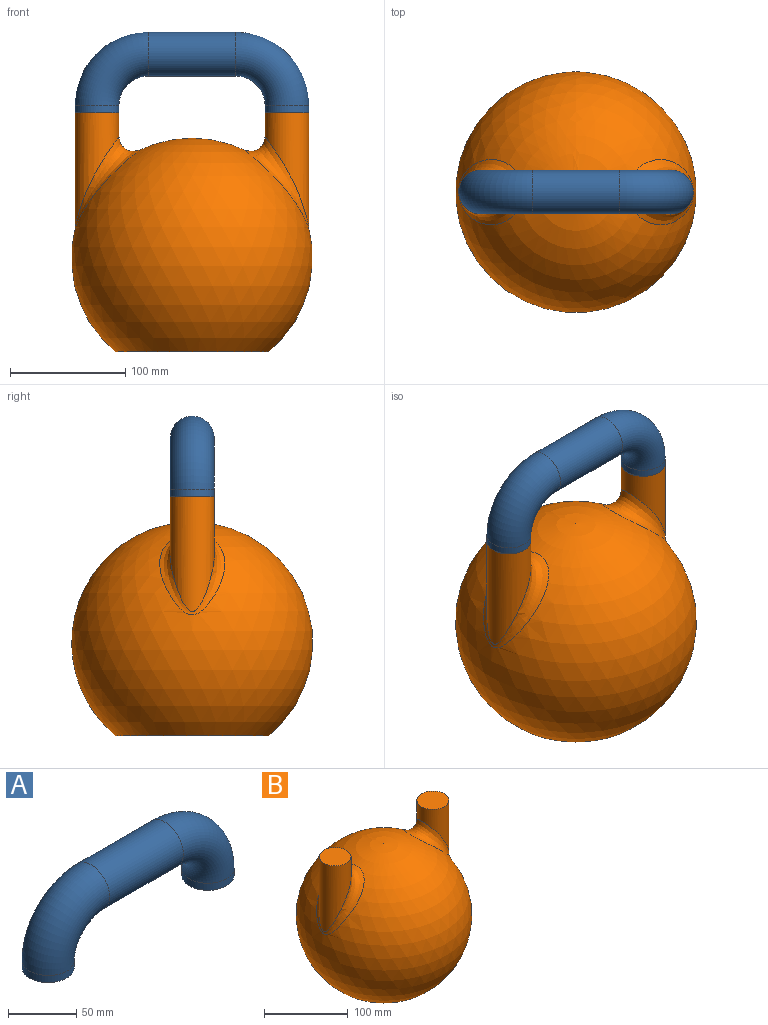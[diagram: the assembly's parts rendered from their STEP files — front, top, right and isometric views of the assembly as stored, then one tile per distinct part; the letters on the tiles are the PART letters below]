
ASSEMBLY  parts=2 mates=1
PART A: 7 faces, bbox 213.7x38.1x75.1 mm
  f0: plane 38.1x38.1mm, normal (0,0,-1), area 1140.1mm2, adj f2
  f1: plane 38.1x38.1mm, normal (0,0,-1), area 1140.1mm2, adj f6
  f2: cylinder r=19.05mm len=38.1mm, axis (0,0,1), area 760.1mm2, adj f0,f3
  f3: torus R=44.45mm, axis (0,1,0), area 8357.3mm2, adj f2,f4
  f4: cylinder r=19.05mm len=76.2mm, axis (1,0,0), area 9120.7mm2, adj f3,f5
  f5: torus R=44.45mm, axis (0,1,0), area 8357.3mm2, adj f4,f6
  f6: cylinder r=19.05mm len=38.1mm, axis (0,0,-1), area 760.1mm2, adj f1,f5
PART B: 8 faces, bbox 209.6x209.6x207.8 mm
  f0: sphere r=104.77mm, area 114109.8mm2, adj f1,f4,f7
  f1: plane 133.35x133.35mm, normal (0,0,-1), area 13966.1mm2, adj f0
  f2: cylinder r=19.05mm len=99.88mm, axis (0,0,-1), area 6523.3mm2, adj f3,f4
  f3: plane 38.1x38.1mm, normal (0,0,1), area 1140.1mm2, adj f2
  f4: bspline ~81.75x56.69mm, area 2989.2mm2, adj f0,f2
  f5: cylinder r=19.05mm len=99.88mm, axis (0,0,-1), area 6523.1mm2, adj f6,f7
  f6: plane 38.1x38.1mm, normal (0,0,1), area 1140.1mm2, adj f5
  f7: bspline ~81.75x56.65mm, area 2989.1mm2, adj f0,f5
PLACE A t=(-329.71,-5.53,158.92)mm
PLACE B t=(-30.06,-3.84,31.92)mm
MATE fastened A.f6 <-> B.f5  axis (0,0,-1) through (52.49,-3.84,158.92)mm
